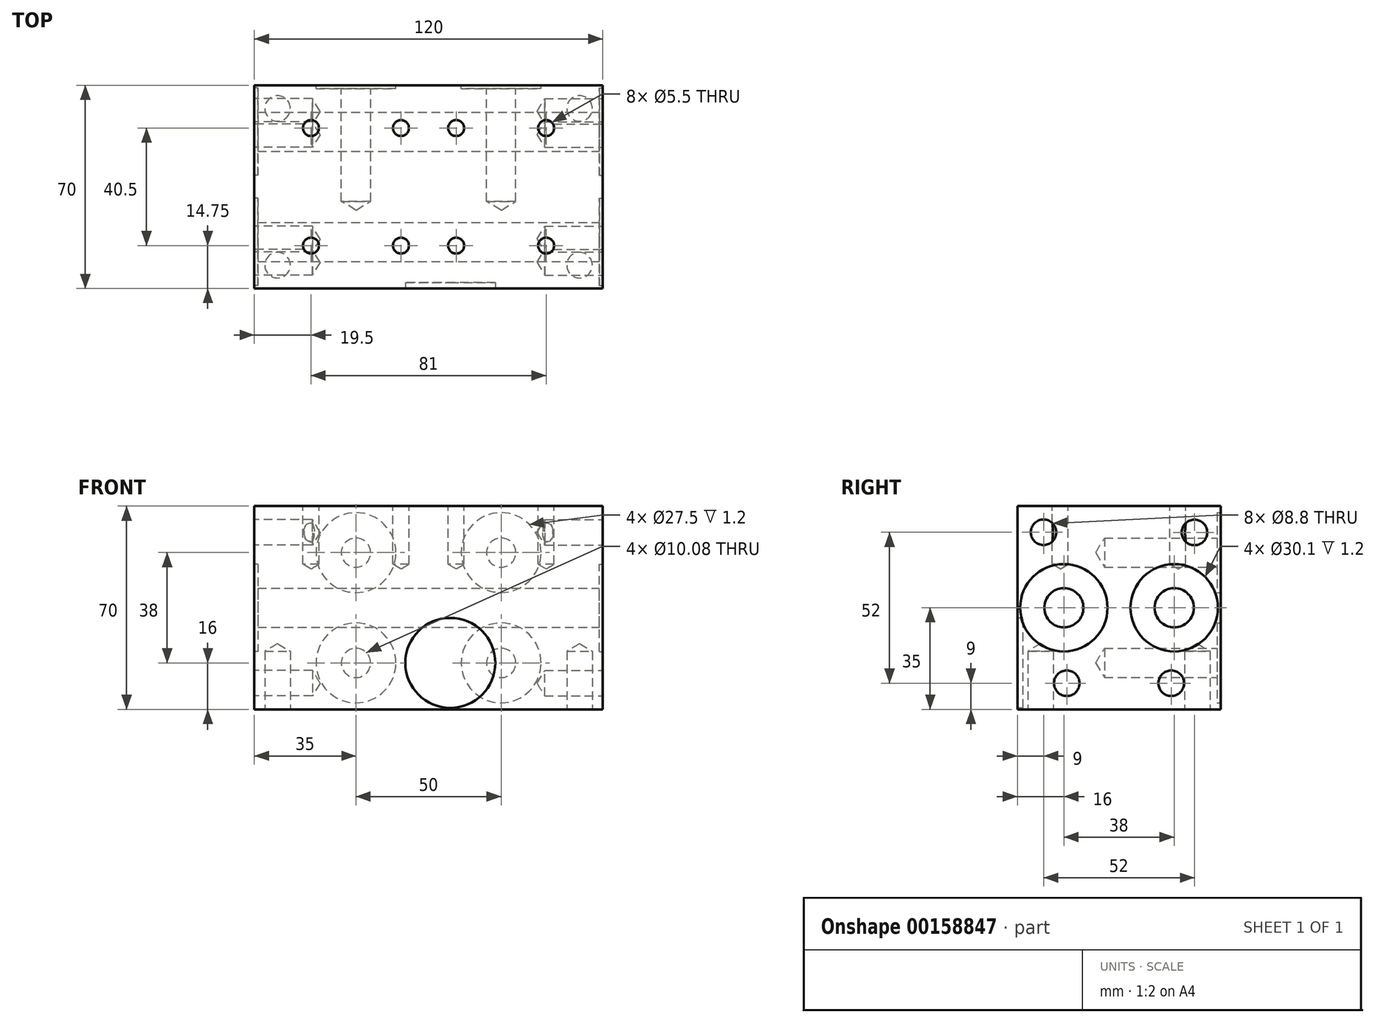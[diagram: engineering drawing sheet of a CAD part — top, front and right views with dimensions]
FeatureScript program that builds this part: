
annotation { "Feature Type Name" : "Feature", "Feature Type Description" : "" }
export const myFeature = defineFeature(function(context is Context, id is Id, definition is map)
    precondition{}
    {
        {
            var Q0;
            Q0=qCreatedBy(makeId("Right.planeOp"),FACE);
            var sketch = newSketch(context, id + "F0", { "sketchPlane" : qUnion([Q0])});
            skLineSegment(sketch, "E0.bottom", {"start": v(-35, -35) * mm, "end": v(35, -35) * mm});
            skLineSegment(sketch, "E0.top", {"start": v(-35, 35) * mm, "end": v(35, 35) * mm});
            skLineSegment(sketch, "E0.left", {"start": v(-35, -35) * mm, "end": v(-35, 35) * mm});
            skLineSegment(sketch, "E0.right", {"start": v(35, -35) * mm, "end": v(35, 35) * mm});
            skPoint(sketch, "E0.middle", {"position": v(0, 0) * mm});
            skSolve(sketch);
        }
        {
            var Q0;
            Q0=makeQuery(id+"F0.imprint","IMPRINT",FACE,{"disambiguationData":[TD([[makeQuery(id+"F0.imprint","IMPRINT",EDGE,{"derivedFrom":sQuery(id+"F0.wireOp",EDGE,"E0.bottom")}),1.0]])]});
            extrude(context, id + "F1", {"entities" : qUnion([Q0]), "depth" : 120 * mm});
        }
        {
            var Q0;
            Q0=makeQuery(id+"F1.opExtrude","CAP_FACE",FACE,{"disambiguationData":[OSD([sQuery(id+"F0.wireOp",EDGE,"E0.bottom"),sQuery(id+"F0.wireOp",EDGE,"E0.top"),sQuery(id+"F0.wireOp",EDGE,"E0.left"),sQuery(id+"F0.wireOp",EDGE,"E0.right")])],"isStart":false});
            var sketch = newSketch(context, id + "F2", { "sketchPlane" : qUnion([Q0])});
            skPoint(sketch, "E1", {"position": v(18, -26) * mm});
            skPoint(sketch, "E2", {"position": v(-18, -26) * mm});
            skPoint(sketch, "E3", {"position": v(-26, 26) * mm});
            skPoint(sketch, "E4", {"position": v(26, 25.94) * mm});
            skCircle(sketch, "E5", {"center": v(-19, 0) * mm, "radius": 15.05 * mm});
            skCircle(sketch, "E6", {"center": v(19, 0) * mm, "radius": 15.05 * mm});
            skSolve(sketch);
        }
        {
            var Q0;
            Q0=sQuery(id+"F2.wireOp",VERTEX,"E5.center");
            var Q1;
            Q1=sQuery(id+"F2.wireOp",VERTEX,"E6.center");
            var Q2;
            Q2=makeQuery(id+"F1.opExtrude","SWEPT_BODY",BODY,{"disambiguationData":[OSD([sQuery(id+"F0.wireOp",EDGE,"E0.bottom"),sQuery(id+"F0.wireOp",EDGE,"E0.top"),sQuery(id+"F0.wireOp",EDGE,"E0.left"),sQuery(id+"F0.wireOp",EDGE,"E0.right")])]});
            hole(context, id + "F3", {"style" : HoleStyle.SIMPLE, "endStyle" : HoleEndStyle.THROUGH, "standardTappedOrClearance" : lookupTablePath({ "standard" : "ANSI", "fit" : "Normal (ASME)", "size" : "1/2", "type" : "Clearance" }), "standardBlindInLast" : lookupTablePath({ "fit" : "Free", "standard" : "ANSI", "size" : "1/2", "type" : "Clearance" }), "holeDiameter" : 13.5 * mm, "locations" : qUnion([Q0, Q1]), "scope" : qUnion([Q2]), "isTappedThrough" : true});
        }
        {
            var Q0;
            Q0=sQuery(id+"F2.wireOp",VERTEX,"E3");
            var Q1;
            Q1=sQuery(id+"F2.wireOp",VERTEX,"E4");
            var Q2;
            Q2=sQuery(id+"F2.wireOp",VERTEX,"E2");
            var Q3;
            Q3=sQuery(id+"F2.wireOp",VERTEX,"E1");
            var Q4;
            Q4=makeQuery(id+"F1.opExtrude","SWEPT_BODY",BODY,{"disambiguationData":[OSD([sQuery(id+"F0.wireOp",EDGE,"E0.bottom"),sQuery(id+"F0.wireOp",EDGE,"E0.top"),sQuery(id+"F0.wireOp",EDGE,"E0.left"),sQuery(id+"F0.wireOp",EDGE,"E0.right")])]});
            hole(context, id + "F4", {"style" : HoleStyle.SIMPLE, "endStyle" : HoleEndStyle.BLIND, "standardTappedOrClearance" : lookupTablePath({ "standard" : "ISO", "fit" : "Normal", "size" : "M8", "type" : "Clearance" }), "standardBlindInLast" : lookupTablePath({ "fit" : "Standard", "standard" : "ISO", "size" : "M8", "type" : "Clearance" }), "holeDiameter" : 8.8 * mm, "holeDepth" : 20 * mm, "locations" : qUnion([Q0, Q1, Q2, Q3]), "scope" : qUnion([Q4])});
        }
        {
            var Q0;
            Q0=qSketchRegion(id+"F2",true);
            extrude(context, id + "F5", {"entities" : qUnion([Q0]), "operationType" : NewBodyOperationType.REMOVE, "oppositeDirection" : true, "depth" : 1.2 * mm});
        }
        {
            var Q0;
            Q0=makeQuery(id+"F1.opExtrude","CAP_FACE",FACE,{"disambiguationData":[OSD([sQuery(id+"F0.wireOp",EDGE,"E0.bottom"),sQuery(id+"F0.wireOp",EDGE,"E0.top"),sQuery(id+"F0.wireOp",EDGE,"E0.left"),sQuery(id+"F0.wireOp",EDGE,"E0.right")])],"isStart":true});
            var sketch = newSketch(context, id + "F6", { "sketchPlane" : qUnion([Q0])});
            skPoint(sketch, "E7", {"position": v(18, -26) * mm});
            skPoint(sketch, "E8", {"position": v(-18, -26) * mm});
            skPoint(sketch, "E9", {"position": v(-26, 25.94) * mm});
            skPoint(sketch, "E10", {"position": v(26, 26) * mm});
            skCircle(sketch, "E11", {"center": v(-19, 0) * mm, "radius": 15.05 * mm});
            skCircle(sketch, "E12", {"center": v(19, 0) * mm, "radius": 15.05 * mm});
            skSolve(sketch);
        }
        {
            var Q0;
            Q0=sQuery(id+"F6.wireOp",VERTEX,"E9");
            var Q1;
            Q1=sQuery(id+"F6.wireOp",VERTEX,"E10");
            var Q2;
            Q2=sQuery(id+"F6.wireOp",VERTEX,"E8");
            var Q3;
            Q3=sQuery(id+"F6.wireOp",VERTEX,"E7");
            var Q4;
            Q4=makeQuery(id+"F1.opExtrude","SWEPT_BODY",BODY,{"disambiguationData":[OSD([sQuery(id+"F0.wireOp",EDGE,"E0.bottom"),sQuery(id+"F0.wireOp",EDGE,"E0.top"),sQuery(id+"F0.wireOp",EDGE,"E0.left"),sQuery(id+"F0.wireOp",EDGE,"E0.right")])]});
            hole(context, id + "F7", {"style" : HoleStyle.SIMPLE, "endStyle" : HoleEndStyle.BLIND, "standardTappedOrClearance" : lookupTablePath({ "standard" : "ISO", "fit" : "Normal", "size" : "M8", "type" : "Clearance" }), "standardBlindInLast" : lookupTablePath({ "fit" : "Standard", "standard" : "ISO", "size" : "M8", "type" : "Clearance" }), "holeDiameter" : 8.8 * mm, "holeDepth" : 20 * mm, "locations" : qUnion([Q0, Q1, Q2, Q3]), "scope" : qUnion([Q4])});
        }
        {
            var Q0;
            Q0=qSketchRegion(id+"F6",true);
            extrude(context, id + "F8", {"entities" : qUnion([Q0]), "operationType" : NewBodyOperationType.REMOVE, "oppositeDirection" : true, "depth" : 1.2 * mm});
        }
        {
            var Q0;
            Q0=makeQuery(id+"F1.opExtrude","SWEPT_FACE",FACE,{"disambiguationData":[OSD([sQuery(id+"F0.wireOp",EDGE,"E0.top")])]});
            var sketch = newSketch(context, id + "F9", { "sketchPlane" : qUnion([Q0])});
            skPoint(sketch, "E13", {"position": v(168.59, 0) * mm});
            skPoint(sketch, "E14", {"position": v(19.5, 20.25) * mm});
            skPoint(sketch, "E15", {"position": v(19.5, -20.25) * mm});
            skPoint(sketch, "E16", {"position": v(50.5, -20.25) * mm});
            skPoint(sketch, "E17", {"position": v(50.5, 20.25) * mm});
            skPoint(sketch, "E18.1.0.0", {"position": v(69.5, 20.25) * mm});
            skPoint(sketch, "E18.1.0.1", {"position": v(69.5, -20.25) * mm});
            skPoint(sketch, "E18.1.0.2", {"position": v(100.5, -20.25) * mm});
            skPoint(sketch, "E18.1.0.3", {"position": v(100.5, 20.25) * mm});
            skLineSegment(sketch, "E18.direction1", {"start": v(19.5, 20.25) * mm, "end": v(69.5, 20.25) * mm, "construction": true});
            skSolve(sketch);
        }
        {
            var Q0;
            Q0=sQuery(id+"F9.wireOp",VERTEX,"E14");
            var Q1;
            Q1=sQuery(id+"F9.wireOp",VERTEX,"E15");
            var Q2;
            Q2=sQuery(id+"F9.wireOp",VERTEX,"E16");
            var Q3;
            Q3=sQuery(id+"F9.wireOp",VERTEX,"E17");
            var Q4;
            Q4=sQuery(id+"F9.wireOp",VERTEX,"E18.1.0.0");
            var Q5;
            Q5=sQuery(id+"F9.wireOp",VERTEX,"E18.1.0.1");
            var Q6;
            Q6=sQuery(id+"F9.wireOp",VERTEX,"E18.1.0.2");
            var Q7;
            Q7=sQuery(id+"F9.wireOp",VERTEX,"E18.1.0.3");
            var Q8;
            Q8=makeQuery(id+"F1.opExtrude","SWEPT_BODY",BODY,{"disambiguationData":[OSD([sQuery(id+"F0.wireOp",EDGE,"E0.bottom"),sQuery(id+"F0.wireOp",EDGE,"E0.top"),sQuery(id+"F0.wireOp",EDGE,"E0.left"),sQuery(id+"F0.wireOp",EDGE,"E0.right")])]});
            hole(context, id + "F10", {"style" : HoleStyle.SIMPLE, "endStyle" : HoleEndStyle.BLIND, "standardTappedOrClearance" : lookupTablePath({ "standard" : "ISO", "fit" : "Normal", "size" : "M5", "type" : "Clearance" }), "standardBlindInLast" : lookupTablePath({ "fit" : "Standard", "standard" : "ISO", "size" : "M5", "type" : "Clearance" }), "holeDiameter" : 5.5 * mm, "holeDepth" : 20 * mm, "locations" : qUnion([Q0, Q1, Q2, Q3, Q4, Q5, Q6, Q7]), "scope" : qUnion([Q8])});
        }
        {
            var Q0;
            Q0=makeQuery(id+"F1.opExtrude","SWEPT_FACE",FACE,{"disambiguationData":[OSD([sQuery(id+"F0.wireOp",EDGE,"E0.bottom")])]});
            var sketch = newSketch(context, id + "F11", { "sketchPlane" : qUnion([Q0])});
            skPoint(sketch, "E19", {"position": v(8, 27) * mm});
            skPoint(sketch, "E20", {"position": v(8, -27) * mm});
            skPoint(sketch, "E21", {"position": v(112, 27) * mm});
            skPoint(sketch, "E22", {"position": v(112, -27) * mm});
            skSolve(sketch);
        }
        {
            var Q0;
            Q0=sQuery(id+"F11.wireOp",VERTEX,"E19");
            var Q1;
            Q1=sQuery(id+"F11.wireOp",VERTEX,"E20");
            var Q2;
            Q2=sQuery(id+"F11.wireOp",VERTEX,"E21");
            var Q3;
            Q3=sQuery(id+"F11.wireOp",VERTEX,"E22");
            var Q4;
            Q4=makeQuery(id+"F1.opExtrude","SWEPT_BODY",BODY,{"disambiguationData":[OSD([sQuery(id+"F0.wireOp",EDGE,"E0.bottom"),sQuery(id+"F0.wireOp",EDGE,"E0.top"),sQuery(id+"F0.wireOp",EDGE,"E0.left"),sQuery(id+"F0.wireOp",EDGE,"E0.right")])]});
            hole(context, id + "F12", {"style" : HoleStyle.SIMPLE, "endStyle" : HoleEndStyle.BLIND, "standardTappedOrClearance" : lookupTablePath({ "standard" : "ISO", "fit" : "Normal", "size" : "M8", "type" : "Clearance" }), "standardBlindInLast" : lookupTablePath({ "fit" : "Standard", "standard" : "ISO", "size" : "M8", "type" : "Clearance" }), "holeDiameter" : 8.8 * mm, "holeDepth" : 20 * mm, "locations" : qUnion([Q0, Q1, Q2, Q3]), "scope" : qUnion([Q4])});
        }
        {
            var Q0;
            Q0=makeQuery(id+"F1.opExtrude","SWEPT_FACE",FACE,{"disambiguationData":[OSD([sQuery(id+"F0.wireOp",EDGE,"E0.right")])]});
            var sketch = newSketch(context, id + "F13", { "sketchPlane" : qUnion([Q0])});
            skPoint(sketch, "E23", {"position": v(-85, 19) * mm});
            skPoint(sketch, "E24", {"position": v(-85, -19) * mm});
            skPoint(sketch, "E25", {"position": v(-35, 19) * mm});
            skPoint(sketch, "E26", {"position": v(-35, -19) * mm});
            skCircle(sketch, "E27", {"center": v(-85, 19) * mm, "radius": 13.75 * mm});
            skCircle(sketch, "E28.0.1.0", {"center": v(-85, -19) * mm, "radius": 13.75 * mm});
            skCircle(sketch, "E28.1.0.0", {"center": v(-35, 19) * mm, "radius": 13.75 * mm});
            skCircle(sketch, "E28.1.1.0", {"center": v(-35, -19) * mm, "radius": 13.75 * mm});
            skLineSegment(sketch, "E28.direction1", {"start": v(-85, 19) * mm, "end": v(-35, 19) * mm, "construction": true});
            skLineSegment(sketch, "E28.direction2", {"start": v(-85, 19) * mm, "end": v(-85, -19) * mm, "construction": true});
            skSolve(sketch);
        }
        {
            var Q0;
            Q0=sQuery(id+"F13.wireOp",VERTEX,"E23");
            var Q1;
            Q1=sQuery(id+"F13.wireOp",VERTEX,"E25");
            var Q2;
            Q2=sQuery(id+"F13.wireOp",VERTEX,"E26");
            var Q3;
            Q3=sQuery(id+"F13.wireOp",VERTEX,"E24");
            var Q4;
            Q4=makeQuery(id+"F1.opExtrude","SWEPT_BODY",BODY,{"disambiguationData":[OSD([sQuery(id+"F0.wireOp",EDGE,"E0.bottom"),sQuery(id+"F0.wireOp",EDGE,"E0.top"),sQuery(id+"F0.wireOp",EDGE,"E0.left"),sQuery(id+"F0.wireOp",EDGE,"E0.right")])]});
            hole(context, id + "F14", {"style" : HoleStyle.SIMPLE, "endStyle" : HoleEndStyle.BLIND, "standardTappedOrClearance" : lookupTablePath({ "standard" : "ANSI", "fit" : "Normal (ASME)", "size" : "3/8", "type" : "Clearance" }), "standardBlindInLast" : lookupTablePath({ "fit" : "Free", "standard" : "ANSI", "size" : "3/8", "type" : "Clearance" }), "holeDiameter" : 10.08 * mm, "holeDepth" : 40 * mm, "locations" : qUnion([Q0, Q1, Q2, Q3]), "scope" : qUnion([Q4])});
        }
        {
            var Q0;
            Q0=qSketchRegion(id+"F13",true);
            extrude(context, id + "F15", {"entities" : qUnion([Q0]), "operationType" : NewBodyOperationType.REMOVE, "oppositeDirection" : true, "depth" : 1.2 * mm});
        }
        {
            var Q0;
            Q0=makeQuery(id+"F1.opExtrude","SWEPT_FACE",FACE,{"disambiguationData":[OSD([sQuery(id+"F0.wireOp",EDGE,"E0.left")])]});
            var sketch = newSketch(context, id + "F16", { "sketchPlane" : qUnion([Q0])});
            skCircle(sketch, "E29", {"center": v(67.5, -19) * mm, "radius": 15.5 * mm});
            skSolve(sketch);
        }
        {
            var Q0;
            Q0=qSketchRegion(id+"F16",true);
            extrude(context, id + "F17", {"entities" : qUnion([Q0]), "operationType" : NewBodyOperationType.REMOVE, "oppositeDirection" : true, "depth" : 2 * mm});
        }
    });
